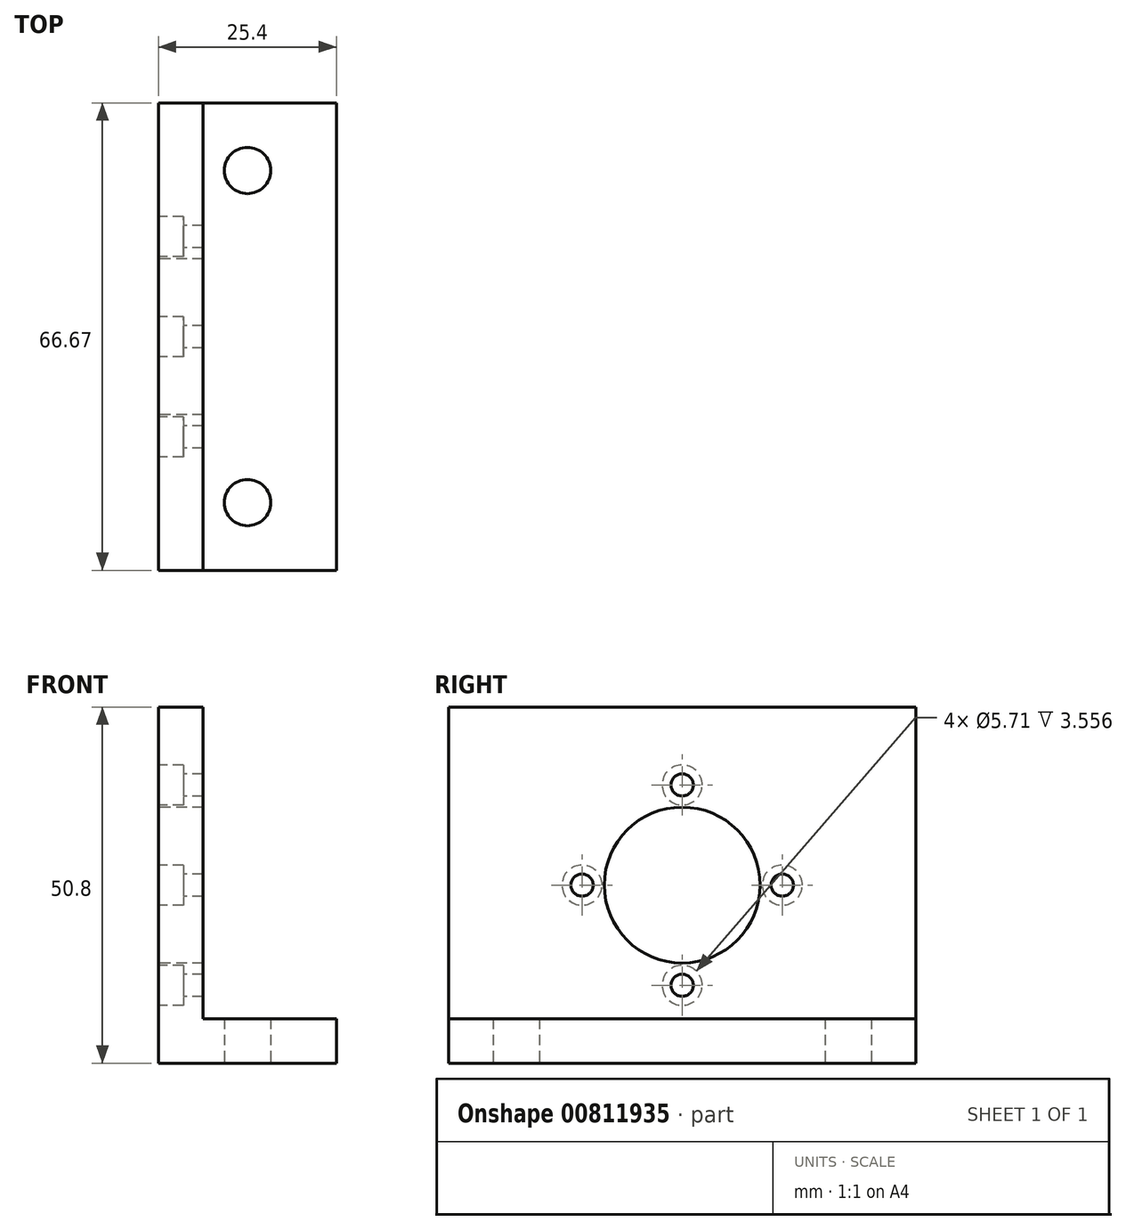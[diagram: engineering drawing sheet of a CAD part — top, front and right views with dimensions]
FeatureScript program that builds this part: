
annotation { "Feature Type Name" : "Feature", "Feature Type Description" : "" }
export const myFeature = defineFeature(function(context is Context, id is Id, definition is map)
    precondition{}
    {
        {
            var Q0;
            Q0=qCreatedBy(makeId("Front.planeOp"),FACE);
            var sketch = newSketch(context, id + "F0", { "sketchPlane" : qUnion([Q0])});
            skLineSegment(sketch, "E0", {"start": v(0, 0) * mm, "end": v(0, 50.8) * mm});
            skLineSegment(sketch, "E1", {"start": v(0, 50.8) * mm, "end": v(6.35, 50.8) * mm});
            skLineSegment(sketch, "E2", {"start": v(6.35, 50.8) * mm, "end": v(6.35, 6.35) * mm});
            skLineSegment(sketch, "E3", {"start": v(6.35, 6.35) * mm, "end": v(25.4, 6.35) * mm});
            skLineSegment(sketch, "E4", {"start": v(25.4, 6.35) * mm, "end": v(25.4, 0) * mm});
            skLineSegment(sketch, "E5", {"start": v(25.4, 0) * mm, "end": v(0, 0) * mm});
            skSolve(sketch);
        }
        {
            var Q0;
            Q0=makeQuery(id+"F0.imprint","IMPRINT",FACE,{"disambiguationData":[TD([[makeQuery(id+"F0.imprint","IMPRINT",EDGE,{"derivedFrom":sQuery(id+"F0.wireOp",EDGE,"E0")}),-1.0]])]});
            extrude(context, id + "F1", {"entities" : qUnion([Q0]), "depth" : 66.67 * mm, "offsetDistance" : 25.4 * mm});
        }
        {
            var Q0;
            Q0=makeQuery(id+"F1.opExtrude","SWEPT_FACE",FACE,{"disambiguationData":[OSD([sQuery(id+"F0.wireOp",EDGE,"E0")])]});
            var sketch = newSketch(context, id + "F2", { "sketchPlane" : qUnion([Q0])});
            skCircle(sketch, "E6", {"center": v(33.34, 25.4) * mm, "radius": 11.11 * mm});
            skPoint(sketch, "E6.centerSnap0", {"position": v(0, 25.4) * mm});
            skPoint(sketch, "E6.centerSnap1", {"position": v(33.34, 50.8) * mm});
            skCircle(sketch, "E7", {"center": v(33.34, 39.69) * mm, "radius": 1.59 * mm});
            skPoint(sketch, "E8.center", {"position": v(0, 0) * mm});
            skCircle(sketch, "E9.1.0", {"center": v(19.05, 25.4) * mm, "radius": 1.59 * mm});
            skCircle(sketch, "E9.2.0", {"center": v(33.34, 11.11) * mm, "radius": 1.59 * mm});
            skCircle(sketch, "E9.3.0", {"center": v(47.63, 25.4) * mm, "radius": 1.59 * mm});
            skSolve(sketch);
        }
        {
            var Q0;
            Q0=makeQuery(id+"F2.imprint","IMPRINT",FACE,{"disambiguationData":[TD([[makeQuery(id+"F2.imprint","IMPRINT",EDGE,{"derivedFrom":sQuery(id+"F2.wireOp",EDGE,"E9.1.0")}),1.0]])]});
            var Q1;
            Q1=makeQuery(id+"F2.imprint","IMPRINT",FACE,{"disambiguationData":[TD([[makeQuery(id+"F2.imprint","IMPRINT",EDGE,{"derivedFrom":sQuery(id+"F2.wireOp",EDGE,"E7")}),1.0]])]});
            var Q2;
            Q2=makeQuery(id+"F2.imprint","IMPRINT",FACE,{"disambiguationData":[TD([[makeQuery(id+"F2.imprint","IMPRINT",EDGE,{"derivedFrom":sQuery(id+"F2.wireOp",EDGE,"E6")}),1.0]])]});
            var Q3;
            Q3=makeQuery(id+"F2.imprint","IMPRINT",FACE,{"disambiguationData":[TD([[makeQuery(id+"F2.imprint","IMPRINT",EDGE,{"derivedFrom":sQuery(id+"F2.wireOp",EDGE,"E9.3.0")}),1.0]])]});
            var Q4;
            Q4=makeQuery(id+"F2.imprint","IMPRINT",FACE,{"disambiguationData":[TD([[makeQuery(id+"F2.imprint","IMPRINT",EDGE,{"derivedFrom":sQuery(id+"F2.wireOp",EDGE,"E9.2.0")}),1.0]])]});
            extrude(context, id + "F3", {"entities" : qUnion([Q0, Q1, Q2, Q3, Q4]), "operationType" : NewBodyOperationType.REMOVE, "endBound" : BoundingType.THROUGH_ALL, "oppositeDirection" : true, "depth" : 25.4 * mm, "offsetDistance" : 25.4 * mm});
        }
        {
            var Q0;
            Q0=makeQuery(id+"F1.opExtrude","SWEPT_FACE",FACE,{"disambiguationData":[OSD([sQuery(id+"F0.wireOp",EDGE,"E0")])]});
            var sketch = newSketch(context, id + "F4", { "sketchPlane" : qUnion([Q0])});
            skCircle(sketch, "E10", {"center": v(33.34, 39.69) * mm, "radius": 2.86 * mm});
            skCircle(sketch, "E11.1.0", {"center": v(19.05, 25.4) * mm, "radius": 2.86 * mm});
            skCircle(sketch, "E11.2.0", {"center": v(33.34, 11.11) * mm, "radius": 2.86 * mm});
            skCircle(sketch, "E11.3.0", {"center": v(47.63, 25.4) * mm, "radius": 2.86 * mm});
            skPoint(sketch, "E11.center", {"position": v(33.34, 25.4) * mm});
            skSolve(sketch);
        }
        {
            var Q0;
            Q0=makeQuery(id+"F4.imprint","IMPRINT",FACE,{"disambiguationData":[TD([[makeQuery(id+"F4.imprint","IMPRINT",EDGE,{"derivedFrom":sQuery(id+"F4.wireOp",EDGE,"E10")}),1.0]])]});
            var Q1;
            Q1=makeQuery(id+"F4.imprint","IMPRINT",FACE,{"disambiguationData":[TD([[makeQuery(id+"F4.imprint","IMPRINT",EDGE,{"derivedFrom":sQuery(id+"F4.wireOp",EDGE,"E11.3.0")}),1.0]])]});
            var Q2;
            Q2=makeQuery(id+"F4.imprint","IMPRINT",FACE,{"disambiguationData":[TD([[makeQuery(id+"F4.imprint","IMPRINT",EDGE,{"derivedFrom":sQuery(id+"F4.wireOp",EDGE,"E11.2.0")}),1.0]])]});
            var Q3;
            Q3=makeQuery(id+"F4.imprint","IMPRINT",FACE,{"disambiguationData":[TD([[makeQuery(id+"F4.imprint","IMPRINT",EDGE,{"derivedFrom":sQuery(id+"F4.wireOp",EDGE,"E11.1.0")}),1.0]])]});
            extrude(context, id + "F5", {"entities" : qUnion([Q0, Q1, Q2, Q3]), "operationType" : NewBodyOperationType.REMOVE, "oppositeDirection" : true, "depth" : 3.56 * mm, "offsetDistance" : 25.4 * mm});
        }
        {
            var Q0;
            Q0=makeQuery(id+"F1.opExtrude","SWEPT_FACE",FACE,{"disambiguationData":[OSD([sQuery(id+"F0.wireOp",EDGE,"E5")])]});
            var sketch = newSketch(context, id + "F6", { "sketchPlane" : qUnion([Q0])});
            skCircle(sketch, "E12", {"center": v(12.7, 9.65) * mm, "radius": 3.3 * mm});
            skCircle(sketch, "E13", {"center": v(12.7, 57.02) * mm, "radius": 3.3 * mm});
            skPoint(sketch, "E13.centerSnap0", {"position": v(12.7, 66.68) * mm});
            skSolve(sketch);
        }
        {
            var Q0;
            Q0=makeQuery(id+"F6.imprint","IMPRINT",FACE,{"disambiguationData":[TD([[makeQuery(id+"F6.imprint","IMPRINT",EDGE,{"derivedFrom":sQuery(id+"F6.wireOp",EDGE,"E12")}),1.0]])]});
            var Q1;
            Q1=makeQuery(id+"F6.imprint","IMPRINT",FACE,{"disambiguationData":[TD([[makeQuery(id+"F6.imprint","IMPRINT",EDGE,{"derivedFrom":sQuery(id+"F6.wireOp",EDGE,"E13")}),1.0]])]});
            extrude(context, id + "F7", {"entities" : qUnion([Q0, Q1]), "operationType" : NewBodyOperationType.REMOVE, "endBound" : BoundingType.THROUGH_ALL, "oppositeDirection" : true, "depth" : 25.4 * mm, "offsetDistance" : 25.4 * mm});
        }
    });
